# Revit family: Шаровой кран с ручкой бабочка (из оцинкованной стали) 2211
name_source: partatom
category: Rohrzubehör
revit_build: Autodesk Revit 2018 (Build: 20190510_1515(x64)
units: mm (PartAtom-declared; Revit-internal decimal feet)

## family parameters
Arbeitsebenenbasiert = Nein
Beim Laden mit Abzugskörper schneiden = Nein
Bemaßung runder Anschluss = Durchmesser verwenden
Gemeinsam genutzt = Nein
Immer vertikal = Ja
OmniClass-Nummer = 23.65.55.14
OmniClass-Titel = Valves for Liquid Services
Teiletyp = Unterbricht

## types (1)
- Шаровой кран с ручкой бабочка (из оцинкованной стали) 2211
    Hersteller = HERZ Armaturen Ges.m.b.H
    S03 = 10 mm  [stored 0.0328084 ft]
    SCRNCODE = 05;10;02
    SCRNSEQ = ARM;ARM_TYP="ABVS";2
    URL = www.herz-armaturen.ru
    W01 = 135.00°
    Внутренняя резьба = в соответствии с ISO 228-1
    Корпус = штампованная латунь в соответствии с  EN 12165, никелированный, CW617N
    Макс. рабочая температура = 150 °C
    Макс. рабочая температура (вода - не пар) = 110 °C
    Макс. рабочее давление = 2500000.0 Pa
    Макс. рабочее давление (соединения) = 1600000.0 Pa
    Мин. рабочая температура = -30 °C
    Мин. рабочая температура (вода) = 1 °C
    Наружная резьба = в соответствии с ISO 7-1
    Область применения = Шаровой кран используется в качестве запорной арматуры в системе. Область применения - системы отопления и холодоснабжения. Рабочие параметры (температура и давление) должны соблюдаться.
    Применение = Шаровые краны используются для перекрытия трубопроводов систем отопления и холодоснабжения. Шаровые краны не должны использоваться в качестве регулирующей арматуры, поэтому они должны быть полностью открыты или закрыты.
    Рукоятка = Ручка бабочка, цвет - красный, из оцинкованной стали
    Среда = Качество теплоносителя в соответствии с ÖNORM H5195 и/или предписаниями VDI 2035.
Разрешается использование смеси этилен или пропиленгликоля в соотношении 25-50% с водой.
    Уплотнение (разъемного соединения с накидной гайкой) DN15-DN25 = EPDM (O-Ring)
    Уплотнение (разъемного соединения с накидной гайкой) DN32-DN50 = KLINGER (плоское уплотнение)
    Уплотнение шара = PTFE
    Уплотнение шпинделя = PTFE
    Шар = штампованная латунь в соответствии с EN 12165, хромированный полнопроходной шар, CW617N
    Шпиндель = латунь в соответствии с EN 12164, CW614N

note: [stored X ft] marks values corroborated as IEEE doubles in the binary element streams (Revit-internal decimal feet)
